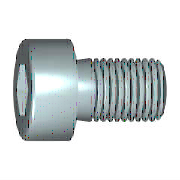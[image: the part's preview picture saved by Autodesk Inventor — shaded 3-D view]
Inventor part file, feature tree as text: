
AUTODESK INVENTOR PART (.ipt)
format: ipt  version: 2022 (Build 260153000, 153)  size: 187,392 bytes
history: native  units: mm (DEFAULTED — no unit token found)
features: sketch x2, other x1, extrude x1, plane x1, fillet x1
ambient origin geometry x7: Origin, YZ Plane, XY Plane, X Axis, Y Axis, Z Axis, Center Point
bodies: Solid1 (feature_tree)
feature tree (6):
  other  "Базовый элемент"
  extrude  "Паз"  Depth=14.0mm
  plane  "Work Plane1"
  fillet  "Fillet2"  Radius=0.429515mm
  sketch  "Эскиз1"
  sketch  "Эскиз2"
